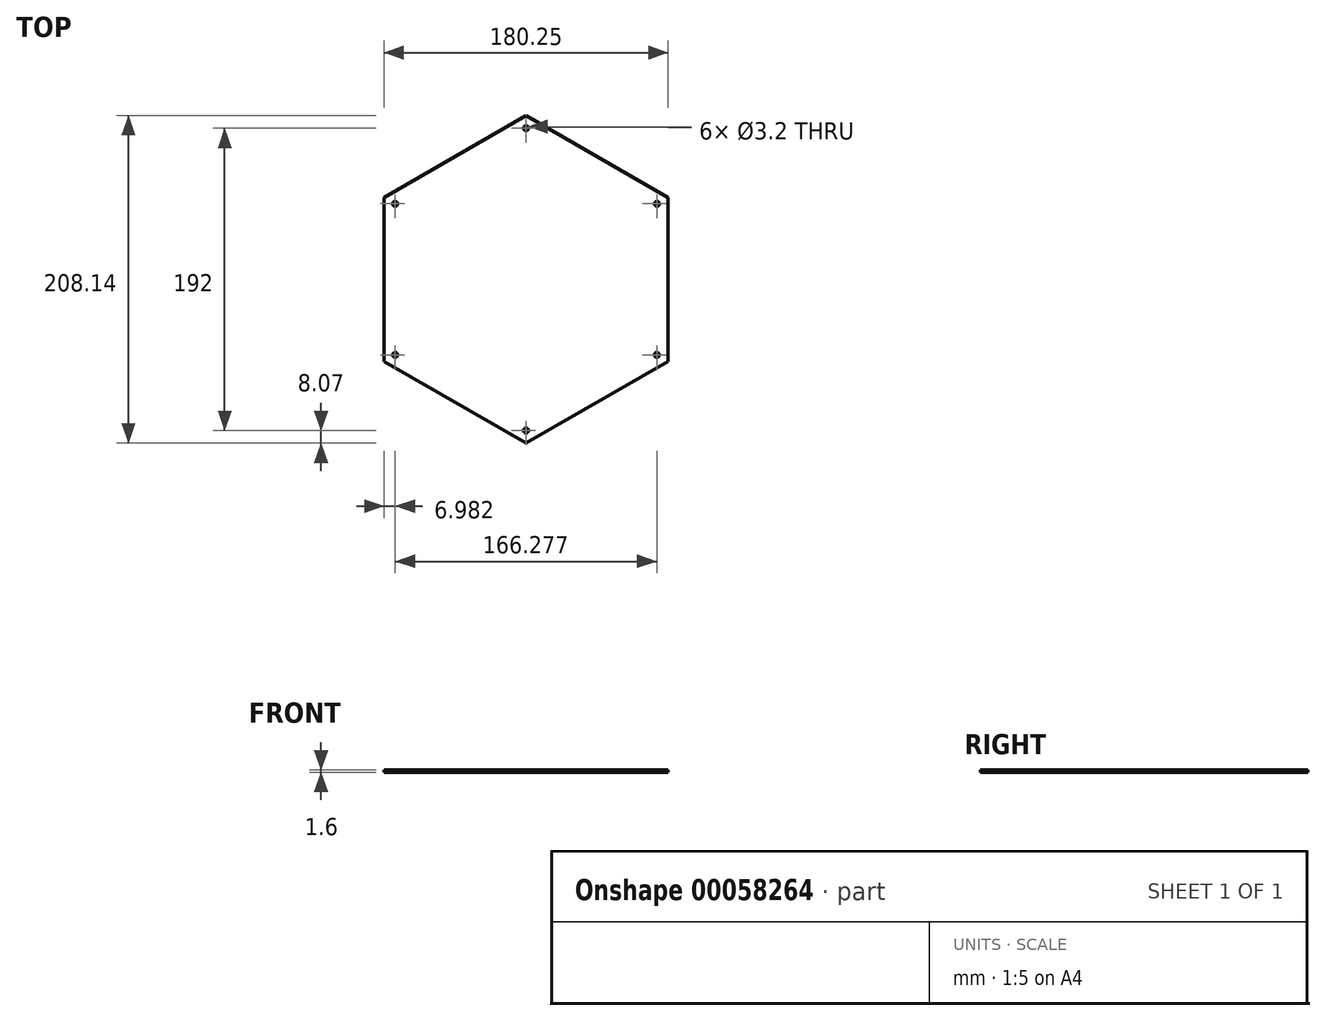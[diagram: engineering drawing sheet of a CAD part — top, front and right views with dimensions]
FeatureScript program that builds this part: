
annotation { "Feature Type Name" : "Feature", "Feature Type Description" : "" }
export const myFeature = defineFeature(function(context is Context, id is Id, definition is map)
    precondition{}
    {
        {
            var Q0;
            Q0=qCreatedBy(makeId("Top.planeOp"),FACE);
            var sketch = newSketch(context, id + "F0", { "sketchPlane" : qUnion([Q0])});
            skLineSegment(sketch, "E0", {"start": v(0, 0) * mm, "end": v(0, 104.07) * mm, "construction": true});
            skLineSegment(sketch, "E1", {"start": v(0, 0) * mm, "end": v(90.12, 52.03) * mm, "construction": true});
            skCircle(sketch, "E2", {"center": v(0, 0) * mm, "radius": 85 * mm, "construction": true});
            skLineSegment(sketch, "E3", {"start": v(0, 104.07) * mm, "end": v(90.13, 52.03) * mm});
            skCircle(sketch, "E4", {"center": v(0, 96) * mm, "radius": 1.6 * mm});
            skCircle(sketch, "E5.1.0", {"center": v(-83.14, 48) * mm, "radius": 1.6 * mm});
            skLineSegment(sketch, "E5.1.1", {"start": v(-90.13, 52.03) * mm, "end": v(0, 104.07) * mm});
            skCircle(sketch, "E5.2.0", {"center": v(-83.14, -48) * mm, "radius": 1.6 * mm});
            skLineSegment(sketch, "E5.2.1", {"start": v(-90.12, -52.03) * mm, "end": v(-90.13, 52.03) * mm});
            skCircle(sketch, "E5.3.0", {"center": v(0, -96) * mm, "radius": 1.6 * mm});
            skLineSegment(sketch, "E5.3.1", {"start": v(0, -104.07) * mm, "end": v(-90.13, -52.03) * mm});
            skCircle(sketch, "E5.4.0", {"center": v(83.14, -48) * mm, "radius": 1.6 * mm});
            skLineSegment(sketch, "E5.4.1", {"start": v(90.12, -52.03) * mm, "end": v(0, -104.07) * mm});
            skCircle(sketch, "E5.5.0", {"center": v(83.14, 48) * mm, "radius": 1.6 * mm});
            skLineSegment(sketch, "E5.5.1", {"start": v(90.12, 52.03) * mm, "end": v(90.13, -52.03) * mm});
            skSolve(sketch);
        }
        {
            var Q0;
            Q0=qSketchRegion(id+"F0",true);
            extrude(context, id + "F1", {"entities" : qUnion([Q0]), "depth" : 1.6 * mm});
        }
    });
